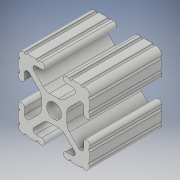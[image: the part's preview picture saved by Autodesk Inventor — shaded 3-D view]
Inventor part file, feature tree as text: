
AUTODESK INVENTOR PART (.ipt)
format: ipt  version: 2018 (Build 220112000, 112)  size: 209,408 bytes
history: native  units: in
note: dims shown in document units (in); Inventor stores cm internally (conversion verified against a paired STEP export)
features: extrude x1, sketch x1
ambient origin geometry x8: Origin, YZ Plane, XZ Plane, XY Plane, X Axis, Y Axis, Z Axis, Center Point
bodies: Solid1 (feature_tree)
feature tree (2):
  extrude  "Extrusion1"  [1 undecoded]
  sketch  "Sketch1"  dims[d0=1.0in d1=0.0in]
note: 1 required parameter value undecoded (feature->parameter linkage not recoverable at this tier; creation-order binding heuristic only, values carry confidence <= 0.55)
